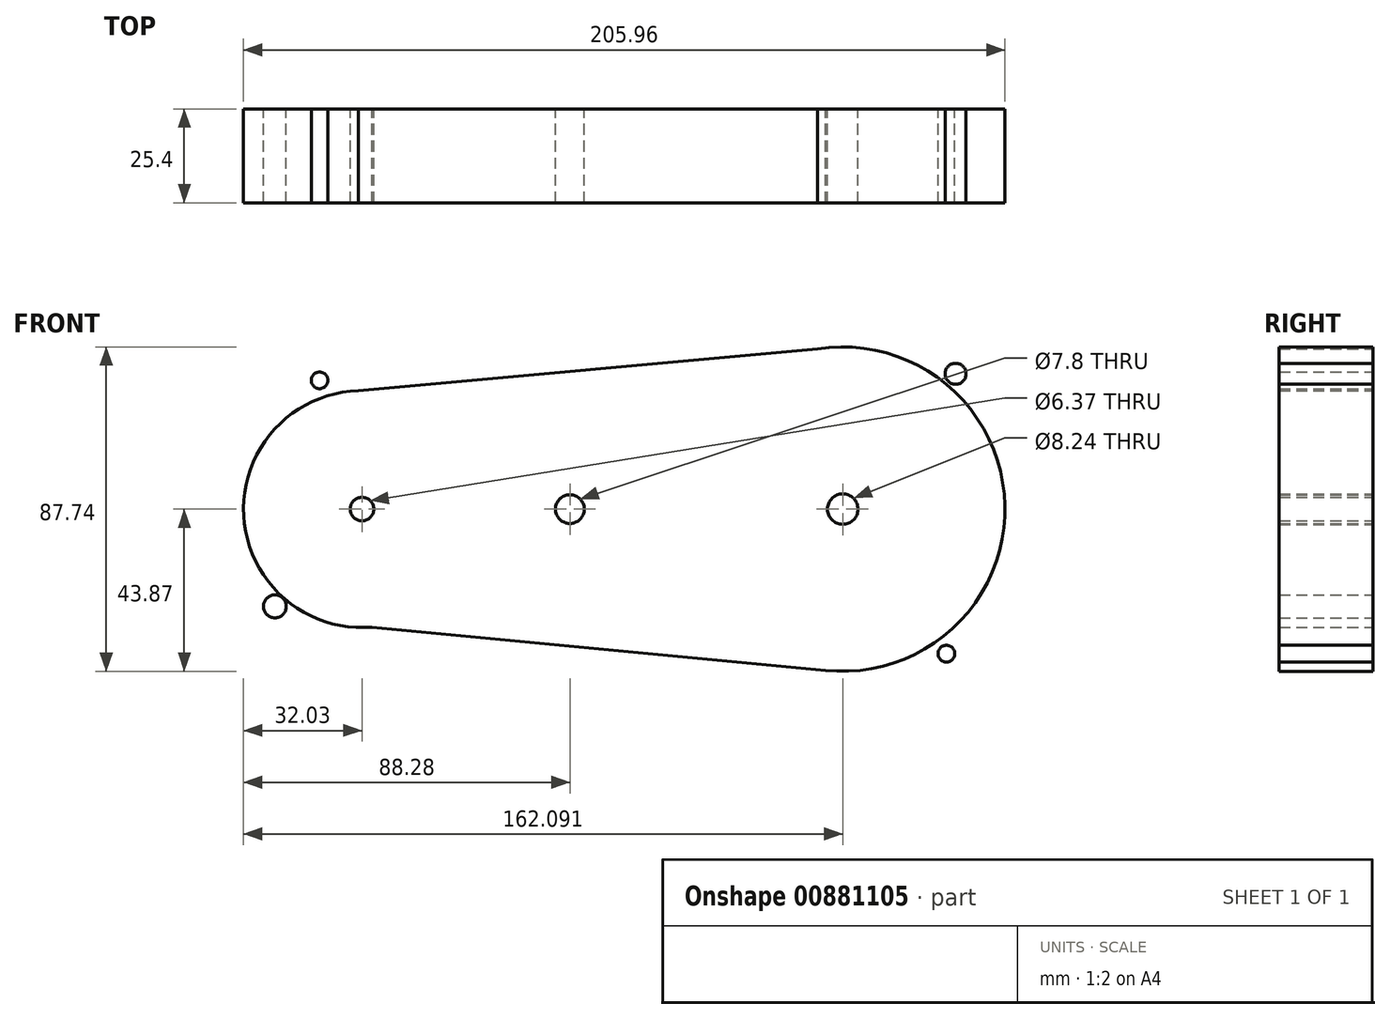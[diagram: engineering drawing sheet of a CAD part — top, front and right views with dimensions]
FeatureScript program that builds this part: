
annotation { "Feature Type Name" : "Feature", "Feature Type Description" : "" }
export const myFeature = defineFeature(function(context is Context, id is Id, definition is map)
    precondition{}
    {
        {
            var Q0;
            Q0=qCreatedBy(makeId("Front.planeOp"),FACE);
            var sketch = newSketch(context, id + "F0", { "sketchPlane" : qUnion([Q0])});
            skCircle(sketch, "E0", {"center": v(-56.25, 0) * mm, "radius": 32.03 * mm});
            skCircle(sketch, "E1", {"center": v(73.81, 0) * mm, "radius": 43.87 * mm});
            skLineSegment(sketch, "E2", {"start": v(-57.22, 32.02) * mm, "end": v(72.67, 43.86) * mm});
            skLineSegment(sketch, "E3", {"start": v(-53.56, -31.92) * mm, "end": v(70.2, -43.72) * mm});
            skCircle(sketch, "E4", {"center": v(-56.25, 0) * mm, "radius": 3.19 * mm});
            skCircle(sketch, "E5", {"center": v(0, 0) * mm, "radius": 3.9 * mm});
            skCircle(sketch, "E6", {"center": v(73.81, 0) * mm, "radius": 4.12 * mm});
            skCircle(sketch, "E7", {"center": v(-67.72, 34.84) * mm, "radius": 2.25 * mm});
            skCircle(sketch, "E8", {"center": v(-79.8, -26.3) * mm, "radius": 3.1 * mm});
            skCircle(sketch, "E9", {"center": v(101.84, -39.1) * mm, "radius": 2.28 * mm});
            skCircle(sketch, "E10", {"center": v(104.33, 36.61) * mm, "radius": 2.84 * mm});
            skSolve(sketch);
        }
        {
            var Q0;
            Q0 = qSketchRegion(id + "F0", true);
            extrude(context, id + "F1", {"entities" : qUnion([Q0]), "depth" : 25.4 * mm, "offsetDistance" : 25.4 * mm});
        }
    });
